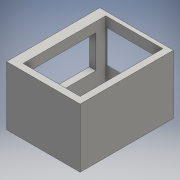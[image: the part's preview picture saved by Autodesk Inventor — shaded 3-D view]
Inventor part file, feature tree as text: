
AUTODESK INVENTOR PART (.ipt)
format: ipt  version: 2016 (Build 200138000, 138)  size: 141,824 bytes
history: native  units: mm
features: extrude x5, sketch x5
ambient origin geometry x8: Origin, YZ Plane, XZ Plane, XY Plane, X Axis, Y Axis, Z Axis, Center Point
bodies: Solid1 (feature_tree)
feature tree (10):
  extrude  "Extrusion1"  Depth=56.0mm
  extrude  "Extrusion2"  Depth=71.0mm
  extrude  "Extrusion4"  Depth=7.5mm
  extrude  "Extrusion5"  Depth=5.0mm
  extrude  "Extrusion6"  Depth=50.0mm
  sketch  "Sketch1"  dims[d0=56.0mm d1=28.0mm]
  sketch  "Sketch2"  dims[d2=71.0mm d3=35.5mm]
  sketch  "Sketch4"  dims[d4=3.0mm d5=7.5mm]
  sketch  "Sketch5"  dims[d7=5.0mm d8=5.0mm]
  sketch  "Sketch6"  dims[d9=45.0mm d10=0.0mm d11=50.0mm d12=25.0mm d13=25.0mm d14=12.5mm d15=10.0mm d16=0.0mm d23=57.5mm d24=30.0mm d25=28.75mm d26=10.0mm d27=2.5mm d28=0.0mm d29=10.0mm d30=30.0mm d31=47.5mm d32=23.75mm d33=2.5mm d34=0.0mm d35=40.0mm d36=20.0mm d37=25.0mm d38=12.5mm d39=2.5mm d40=0.0mm]
